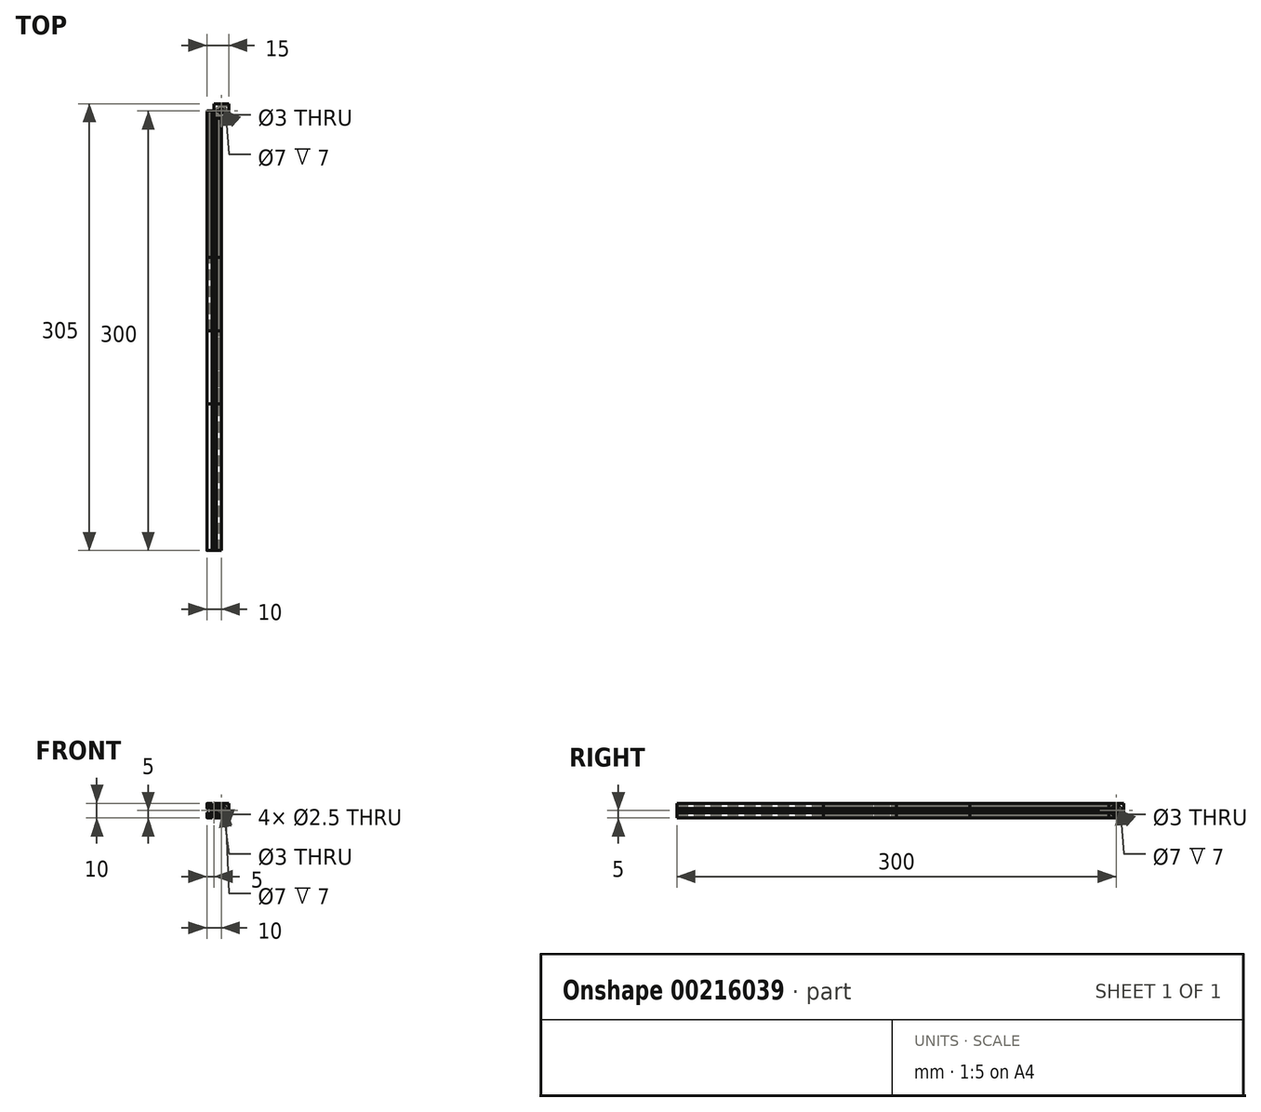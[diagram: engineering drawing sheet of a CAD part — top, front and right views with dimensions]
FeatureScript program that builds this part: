
annotation { "Feature Type Name" : "Feature", "Feature Type Description" : "" }
export const myFeature = defineFeature(function(context is Context, id is Id, definition is map)
    precondition{}
    {
        {
            var Q0;
            Q0=qCreatedBy(makeId("Front.planeOp"),FACE);
            var sketch = newSketch(context, id + "F0", { "sketchPlane" : qUnion([Q0])});
            skCircle(sketch, "E0", {"center": v(0, 0) * mm, "radius": 1.25 * mm});
            skLineSegment(sketch, "E1", {"start": v(-1, 2) * mm, "end": v(1, 2) * mm});
            skLineSegment(sketch, "E2", {"start": v(3.12, 3.64) * mm, "end": v(1, 2) * mm});
            skLineSegment(sketch, "E3", {"start": v(1.7, 4) * mm, "end": v(3, 4) * mm});
            skLineSegment(sketch, "E4", {"start": v(1.5, 4.2) * mm, "end": v(1.5, 4.8) * mm});
            skLineSegment(sketch, "E5", {"start": v(1.7, 5) * mm, "end": v(4.8, 5) * mm});
            skLineSegment(sketch, "E6", {"start": v(5, 4.8) * mm, "end": v(5, 1.7) * mm});
            skLineSegment(sketch, "E7", {"start": v(4.8, 1.5) * mm, "end": v(4.2, 1.5) * mm});
            skLineSegment(sketch, "E8", {"start": v(4, 1.7) * mm, "end": v(4, 3) * mm});
            skLineSegment(sketch, "E9", {"start": v(3.64, 3.12) * mm, "end": v(2, 1) * mm});
            skLineSegment(sketch, "E10", {"start": v(-6.94, 0) * mm, "end": v(7.3, 0) * mm, "construction": true});
            skPoint(sketch, "E11.visualSharp", {"position": v(5, 5) * mm});
            skArc(sketch, "E11.filletArc", {"start": v(5, 4.8) * mm, "mid": v(4.94, 4.94) * mm, "end": v(4.8, 5) * mm});
            skPoint(sketch, "E12.visualSharp", {"position": v(5, 1.5) * mm});
            skArc(sketch, "E12.filletArc", {"start": v(4.8, 1.5) * mm, "mid": v(4.94, 1.56) * mm, "end": v(5, 1.7) * mm});
            skPoint(sketch, "E13.visualSharp", {"position": v(4, 1.5) * mm});
            skArc(sketch, "E13.filletArc", {"start": v(4, 1.7) * mm, "mid": v(4.06, 1.56) * mm, "end": v(4.2, 1.5) * mm});
            skPoint(sketch, "E14.visualSharp", {"position": v(1.5, 5) * mm});
            skArc(sketch, "E14.filletArc", {"start": v(1.7, 5) * mm, "mid": v(1.56, 4.94) * mm, "end": v(1.5, 4.8) * mm});
            skPoint(sketch, "E15.visualSharp", {"position": v(1.5, 4) * mm});
            skArc(sketch, "E15.filletArc", {"start": v(1.5, 4.2) * mm, "mid": v(1.56, 4.06) * mm, "end": v(1.7, 4) * mm});
            skLineSegment(sketch, "E16", {"start": v(0, -7.05) * mm, "end": v(0, 7.43) * mm, "construction": true});
            skPoint(sketch, "E17.visualSharp", {"position": v(3.58, 4) * mm});
            skArc(sketch, "E17.filletArc", {"start": v(3.12, 3.64) * mm, "mid": v(3.19, 3.86) * mm, "end": v(3, 4) * mm});
            skPoint(sketch, "E18.visualSharp", {"position": v(4, 3.58) * mm});
            skArc(sketch, "E18.filletArc", {"start": v(4, 3) * mm, "mid": v(3.86, 3.19) * mm, "end": v(3.64, 3.12) * mm});
            skLineSegment(sketch, "E19.1.0", {"start": v(-3.64, 3.12) * mm, "end": v(-2, 1) * mm});
            skLineSegment(sketch, "E19.1.1", {"start": v(-1.7, 4) * mm, "end": v(-3, 4) * mm});
            skPoint(sketch, "E19.1.2", {"position": v(-3.58, 4) * mm});
            skLineSegment(sketch, "E19.1.3", {"start": v(-4.8, 5) * mm, "end": v(-1.7, 5) * mm});
            skPoint(sketch, "E19.1.4", {"position": v(-5, 5) * mm});
            skLineSegment(sketch, "E19.1.5", {"start": v(-3.12, 3.64) * mm, "end": v(-1, 2) * mm});
            skLineSegment(sketch, "E19.1.6", {"start": v(-1.5, 4.8) * mm, "end": v(-1.5, 4.2) * mm});
            skPoint(sketch, "E19.1.7", {"position": v(-5, 1.5) * mm});
            skPoint(sketch, "E19.1.8", {"position": v(-4, 1.5) * mm});
            skLineSegment(sketch, "E19.1.9", {"start": v(-5, 1.7) * mm, "end": v(-5, 4.8) * mm});
            skPoint(sketch, "E19.1.10", {"position": v(-1.5, 4) * mm});
            skPoint(sketch, "E19.1.11", {"position": v(-1.5, 5) * mm});
            skLineSegment(sketch, "E19.1.12", {"start": v(-4.2, 1.5) * mm, "end": v(-4.8, 1.5) * mm});
            skPoint(sketch, "E19.1.13", {"position": v(-4, 3.58) * mm});
            skArc(sketch, "E19.1.14", {"start": v(-3, 4) * mm, "mid": v(-3.19, 3.86) * mm, "end": v(-3.12, 3.64) * mm});
            skLineSegment(sketch, "E19.1.15", {"start": v(-4, 1.7) * mm, "end": v(-4, 3) * mm});
            skLineSegment(sketch, "E19.1.16", {"start": v(-2, -1) * mm, "end": v(-2, 1) * mm});
            skArc(sketch, "E19.1.17", {"start": v(-3.64, 3.12) * mm, "mid": v(-3.86, 3.19) * mm, "end": v(-4, 3) * mm});
            skArc(sketch, "E19.1.18", {"start": v(-1.5, 4.8) * mm, "mid": v(-1.56, 4.94) * mm, "end": v(-1.7, 5) * mm});
            skArc(sketch, "E19.1.19", {"start": v(-1.7, 4) * mm, "mid": v(-1.56, 4.06) * mm, "end": v(-1.5, 4.2) * mm});
            skArc(sketch, "E19.1.20", {"start": v(-5, 1.7) * mm, "mid": v(-4.94, 1.56) * mm, "end": v(-4.8, 1.5) * mm});
            skArc(sketch, "E19.1.21", {"start": v(-4.2, 1.5) * mm, "mid": v(-4.06, 1.56) * mm, "end": v(-4, 1.7) * mm});
            skArc(sketch, "E19.1.22", {"start": v(-4.8, 5) * mm, "mid": v(-4.94, 4.94) * mm, "end": v(-5, 4.8) * mm});
            skLineSegment(sketch, "E19.2.0", {"start": v(-3.12, -3.64) * mm, "end": v(-1, -2) * mm});
            skLineSegment(sketch, "E19.2.1", {"start": v(-4, -1.7) * mm, "end": v(-4, -3) * mm});
            skPoint(sketch, "E19.2.2", {"position": v(-4, -3.58) * mm});
            skLineSegment(sketch, "E19.2.3", {"start": v(-5, -4.8) * mm, "end": v(-5, -1.7) * mm});
            skPoint(sketch, "E19.2.4", {"position": v(-5, -5) * mm});
            skLineSegment(sketch, "E19.2.5", {"start": v(-3.64, -3.12) * mm, "end": v(-2, -1) * mm});
            skLineSegment(sketch, "E19.2.6", {"start": v(-4.8, -1.5) * mm, "end": v(-4.2, -1.5) * mm});
            skPoint(sketch, "E19.2.7", {"position": v(-1.5, -5) * mm});
            skPoint(sketch, "E19.2.8", {"position": v(-1.5, -4) * mm});
            skLineSegment(sketch, "E19.2.9", {"start": v(-1.7, -5) * mm, "end": v(-4.8, -5) * mm});
            skPoint(sketch, "E19.2.10", {"position": v(-4, -1.5) * mm});
            skPoint(sketch, "E19.2.11", {"position": v(-5, -1.5) * mm});
            skLineSegment(sketch, "E19.2.12", {"start": v(-1.5, -4.2) * mm, "end": v(-1.5, -4.8) * mm});
            skPoint(sketch, "E19.2.13", {"position": v(-3.58, -4) * mm});
            skArc(sketch, "E19.2.14", {"start": v(-4, -3) * mm, "mid": v(-3.86, -3.19) * mm, "end": v(-3.64, -3.12) * mm});
            skLineSegment(sketch, "E19.2.15", {"start": v(-1.7, -4) * mm, "end": v(-3, -4) * mm});
            skLineSegment(sketch, "E19.2.16", {"start": v(1, -2) * mm, "end": v(-1, -2) * mm});
            skArc(sketch, "E19.2.17", {"start": v(-3.12, -3.64) * mm, "mid": v(-3.19, -3.86) * mm, "end": v(-3, -4) * mm});
            skArc(sketch, "E19.2.18", {"start": v(-4.8, -1.5) * mm, "mid": v(-4.94, -1.56) * mm, "end": v(-5, -1.7) * mm});
            skArc(sketch, "E19.2.19", {"start": v(-4, -1.7) * mm, "mid": v(-4.06, -1.56) * mm, "end": v(-4.2, -1.5) * mm});
            skArc(sketch, "E19.2.20", {"start": v(-1.7, -5) * mm, "mid": v(-1.56, -4.94) * mm, "end": v(-1.5, -4.8) * mm});
            skArc(sketch, "E19.2.21", {"start": v(-1.5, -4.2) * mm, "mid": v(-1.56, -4.06) * mm, "end": v(-1.7, -4) * mm});
            skArc(sketch, "E19.2.22", {"start": v(-5, -4.8) * mm, "mid": v(-4.94, -4.94) * mm, "end": v(-4.8, -5) * mm});
            skLineSegment(sketch, "E19.3.0", {"start": v(3.64, -3.12) * mm, "end": v(2, -1) * mm});
            skLineSegment(sketch, "E19.3.1", {"start": v(1.7, -4) * mm, "end": v(3, -4) * mm});
            skPoint(sketch, "E19.3.2", {"position": v(3.58, -4) * mm});
            skLineSegment(sketch, "E19.3.3", {"start": v(4.8, -5) * mm, "end": v(1.7, -5) * mm});
            skPoint(sketch, "E19.3.4", {"position": v(5, -5) * mm});
            skLineSegment(sketch, "E19.3.5", {"start": v(3.12, -3.64) * mm, "end": v(1, -2) * mm});
            skLineSegment(sketch, "E19.3.6", {"start": v(1.5, -4.8) * mm, "end": v(1.5, -4.2) * mm});
            skPoint(sketch, "E19.3.7", {"position": v(5, -1.5) * mm});
            skPoint(sketch, "E19.3.8", {"position": v(4, -1.5) * mm});
            skLineSegment(sketch, "E19.3.9", {"start": v(5, -1.7) * mm, "end": v(5, -4.8) * mm});
            skPoint(sketch, "E19.3.10", {"position": v(1.5, -4) * mm});
            skPoint(sketch, "E19.3.11", {"position": v(1.5, -5) * mm});
            skLineSegment(sketch, "E19.3.12", {"start": v(4.2, -1.5) * mm, "end": v(4.8, -1.5) * mm});
            skPoint(sketch, "E19.3.13", {"position": v(4, -3.58) * mm});
            skArc(sketch, "E19.3.14", {"start": v(3, -4) * mm, "mid": v(3.19, -3.86) * mm, "end": v(3.12, -3.64) * mm});
            skLineSegment(sketch, "E19.3.15", {"start": v(4, -1.7) * mm, "end": v(4, -3) * mm});
            skLineSegment(sketch, "E19.3.16", {"start": v(2, 1) * mm, "end": v(2, -1) * mm});
            skArc(sketch, "E19.3.17", {"start": v(3.64, -3.12) * mm, "mid": v(3.86, -3.19) * mm, "end": v(4, -3) * mm});
            skArc(sketch, "E19.3.18", {"start": v(1.5, -4.8) * mm, "mid": v(1.56, -4.94) * mm, "end": v(1.7, -5) * mm});
            skArc(sketch, "E19.3.19", {"start": v(1.7, -4) * mm, "mid": v(1.56, -4.06) * mm, "end": v(1.5, -4.2) * mm});
            skArc(sketch, "E19.3.20", {"start": v(5, -1.7) * mm, "mid": v(4.94, -1.56) * mm, "end": v(4.8, -1.5) * mm});
            skArc(sketch, "E19.3.21", {"start": v(4.2, -1.5) * mm, "mid": v(4.06, -1.56) * mm, "end": v(4, -1.7) * mm});
            skArc(sketch, "E19.3.22", {"start": v(4.8, -5) * mm, "mid": v(4.94, -4.94) * mm, "end": v(5, -4.8) * mm});
            skSolve(sketch);
        }
        {
            var Q0;
            Q0=makeQuery(id+"F0.imprint","IMPRINT",FACE,{"disambiguationData":[TD([[makeQuery(id+"F0.imprint","IMPRINT",EDGE,{"derivedFrom":sQuery(id+"F0.wireOp",EDGE,"E0")}),-1.0]])]});
            extrude(context, id + "F1", {"entities" : qUnion([Q0]), "depth" : 300 * mm});
        }
        {
            var Q0;
            Q0 = qSketchRegion(id + "F0", true);
            extrude(context, id + "F2", {"entities" : qUnion([Q0]), "depth" : 200 * mm});
        }
        {
            var Q0;
            Q0=qCreatedBy(makeId("Right.planeOp"),FACE);
            var sketch = newSketch(context, id + "F3", { "sketchPlane" : qUnion([Q0])});
            skLineSegment(sketch, "E20.bottom", {"start": v(5, -5) * mm, "end": v(-5, -5) * mm});
            skLineSegment(sketch, "E20.top", {"start": v(5, 5) * mm, "end": v(-5, 5) * mm});
            skLineSegment(sketch, "E20.left", {"start": v(5, -5) * mm, "end": v(5, 5) * mm});
            skLineSegment(sketch, "E20.right", {"start": v(-5, -5) * mm, "end": v(-5, 5) * mm});
            skPoint(sketch, "E20.middle", {"position": v(0, 0) * mm});
            skSolve(sketch);
        }
        {
            var Q0;
            Q0=makeQuery(id+"F3.imprint","IMPRINT",FACE,{"disambiguationData":[TD([[makeQuery(id+"F3.imprint","IMPRINT",EDGE,{"derivedFrom":sQuery(id+"F3.wireOp",EDGE,"E20.bottom")}),-1.0]])]});
            extrude(context, id + "F4", {"entities" : qUnion([Q0]), "depth" : 10 * mm});
        }
        {
            var Q0;
            Q0=makeQuery(id+"F4.opExtrude","SWEPT_FACE",FACE,{"disambiguationData":[OSD([sQuery(id+"F3.wireOp",EDGE,"E20.left")])]});
            var sketch = newSketch(context, id + "F5", { "sketchPlane" : qUnion([Q0])});
            skCircle(sketch, "E21", {"center": v(-5, 0) * mm, "radius": 1.5 * mm});
            skPoint(sketch, "E21.centerSnap0", {"position": v(-5, 5) * mm});
            skPoint(sketch, "E21.centerSnap1", {"position": v(-10, 0) * mm});
            skSolve(sketch);
        }
        {
            var Q0;
            Q0 = qSketchRegion(id + "F5", true);
            extrude(context, id + "F6", {"entities" : qUnion([Q0]), "operationType" : NewBodyOperationType.REMOVE, "endBound" : BoundingType.THROUGH_ALL, "oppositeDirection" : true, "depth" : 25 * mm});
        }
        {
            var Q0;
            Q0=makeQuery(id+"F4.opExtrude","SWEPT_FACE",FACE,{"disambiguationData":[OSD([sQuery(id+"F3.wireOp",EDGE,"E20.top")])]});
            var sketch = newSketch(context, id + "F7", { "sketchPlane" : qUnion([Q0])});
            skCircle(sketch, "E22", {"center": v(5, 0) * mm, "radius": 1.5 * mm});
            skPoint(sketch, "E22.centerSnap0", {"position": v(5, 5) * mm});
            skPoint(sketch, "E22.centerSnap1", {"position": v(0, 0) * mm});
            skSolve(sketch);
        }
        {
            var Q0;
            Q0 = qSketchRegion(id + "F7", true);
            extrude(context, id + "F8", {"entities" : qUnion([Q0]), "operationType" : NewBodyOperationType.REMOVE, "endBound" : BoundingType.THROUGH_ALL, "oppositeDirection" : true, "depth" : 25 * mm});
        }
        {
            var Q0;
            Q0=makeQuery(id+"F4.opExtrude","CAP_FACE",FACE,{"disambiguationData":[OSD([sQuery(id+"F3.wireOp",EDGE,"E20.bottom"),sQuery(id+"F3.wireOp",EDGE,"E20.top"),sQuery(id+"F3.wireOp",EDGE,"E20.left"),sQuery(id+"F3.wireOp",EDGE,"E20.right")])],"isStart":true});
            var sketch = newSketch(context, id + "F9", { "sketchPlane" : qUnion([Q0])});
            skCircle(sketch, "E23", {"center": v(0, 0) * mm, "radius": 1.5 * mm});
            skSolve(sketch);
        }
        {
            var Q0;
            Q0 = qSketchRegion(id + "F9", true);
            extrude(context, id + "F10", {"entities" : qUnion([Q0]), "operationType" : NewBodyOperationType.REMOVE, "endBound" : BoundingType.THROUGH_ALL, "oppositeDirection" : true, "depth" : 25 * mm});
        }
        {
            var Q0;
            Q0=makeQuery(id+"F4.opExtrude","SWEPT_FACE",FACE,{"disambiguationData":[OSD([sQuery(id+"F3.wireOp",EDGE,"E20.right")])]});
            var sketch = newSketch(context, id + "F11", { "sketchPlane" : qUnion([Q0])});
            skCircle(sketch, "E24", {"center": v(5, 0) * mm, "radius": 3.5 * mm});
            skSolve(sketch);
        }
        {
            var Q0;
            Q0 = qSketchRegion(id + "F11", true);
            extrude(context, id + "F12", {"entities" : qUnion([Q0]), "operationType" : NewBodyOperationType.REMOVE, "oppositeDirection" : true, "depth" : 7 * mm});
        }
        {
            var Q0;
            Q0=makeQuery(id+"F4.opExtrude","SWEPT_FACE",FACE,{"disambiguationData":[OSD([sQuery(id+"F3.wireOp",EDGE,"E20.bottom")])]});
            var sketch = newSketch(context, id + "F13", { "sketchPlane" : qUnion([Q0])});
            skCircle(sketch, "E25", {"center": v(5, 0) * mm, "radius": 3.5 * mm});
            skSolve(sketch);
        }
        {
            var Q0;
            Q0 = qSketchRegion(id + "F13", true);
            extrude(context, id + "F14", {"entities" : qUnion([Q0]), "operationType" : NewBodyOperationType.REMOVE, "oppositeDirection" : true, "depth" : 7 * mm});
        }
        {
            var Q0;
            Q0=makeQuery(id+"F4.opExtrude","CAP_FACE",FACE,{"disambiguationData":[OSD([sQuery(id+"F3.wireOp",EDGE,"E20.bottom"),sQuery(id+"F3.wireOp",EDGE,"E20.top"),sQuery(id+"F3.wireOp",EDGE,"E20.left"),sQuery(id+"F3.wireOp",EDGE,"E20.right")])],"isStart":false});
            var sketch = newSketch(context, id + "F15", { "sketchPlane" : qUnion([Q0])});
            skCircle(sketch, "E26", {"center": v(0, 0) * mm, "radius": 3.5 * mm});
            skSolve(sketch);
        }
        {
            var Q0;
            Q0 = qSketchRegion(id + "F15", true);
            extrude(context, id + "F16", {"entities" : qUnion([Q0]), "operationType" : NewBodyOperationType.REMOVE, "oppositeDirection" : true, "depth" : 7 * mm});
        }
        {
            var Q0;
            Q0=makeQuery(id+"F0.imprint","IMPRINT",FACE,{"disambiguationData":[TD([[makeQuery(id+"F0.imprint","IMPRINT",EDGE,{"derivedFrom":sQuery(id+"F0.wireOp",EDGE,"E0")}),-1.0]])]});
            extrude(context, id + "F17", {"entities" : qUnion([Q0]), "depth" : 100 * mm});
        }
        {
            var Q0;
            Q0=makeQuery(id+"F0.imprint","IMPRINT",FACE,{"disambiguationData":[TD([[makeQuery(id+"F0.imprint","IMPRINT",EDGE,{"derivedFrom":sQuery(id+"F0.wireOp",EDGE,"E0")}),-1.0]])]});
            extrude(context, id + "F18", {"entities" : qUnion([Q0]), "depth" : 150 * mm});
        }
    });
